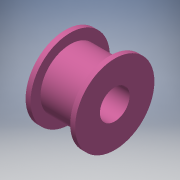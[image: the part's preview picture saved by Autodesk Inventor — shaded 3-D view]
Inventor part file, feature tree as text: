
AUTODESK INVENTOR PART (.ipt)
format: ipt  version: 2017 SP1 (Build 210196100, 196)  size: 125,952 bytes
history: native  units: in
note: dims shown in document units (in); Inventor stores cm internally (conversion verified against a paired STEP export)
features: extrude x4, sketch x4
ambient origin geometry x8: Origin, YZ Plane, XZ Plane, XY Plane, X Axis, Y Axis, Z Axis, Center Point
bodies: Solid1 (feature_tree)
feature tree (8):
  extrude  "Extrusion1"  Depth=0.375in
  extrude  "Extrusion2"  Depth=0.5in
  extrude  "Extrusion3"  Depth=0.0625in TaperAngle=0.0deg
  extrude  "Extrusion4"  Depth=0.375in TaperAngle=0.0deg
  sketch  "Sketch1"  dims[d0=0.75in d2=0.375in]
  sketch  "Sketch2"  dims[d4=0.5in d5=0.0in d6=0.125in]
  sketch  "Sketch3"  dims[d7=0.0625in d8=0.0in d9=0.0625in d10=0.0in]
  sketch  "Sketch4"  dims[d11=0.1875in d12=0.375in d13=0.0in]
